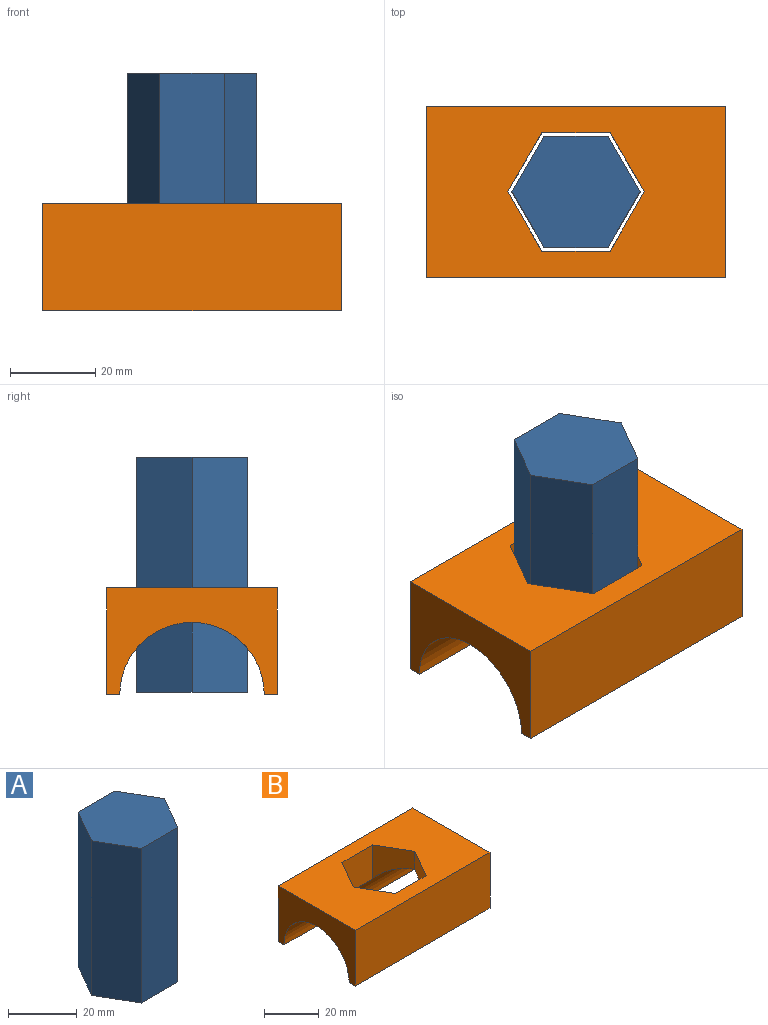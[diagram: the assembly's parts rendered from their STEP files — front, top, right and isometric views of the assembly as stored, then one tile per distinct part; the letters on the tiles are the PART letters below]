
ASSEMBLY  parts=2 mates=3
PART A: 8 faces, bbox 30x26x55 mm
  f0: plane 55x12.99mm, normal (0.87,-0.5,0), area 825mm2, adj f1,f5,f6,f7
  f1: plane 55x12.99mm, normal (0.87,0.5,0), area 825mm2, adj f0,f2,f6,f7
  f2: plane 55x15mm, normal (0,1,0), area 825mm2, adj f1,f3,f6,f7
  f3: plane 55x12.99mm, normal (-0.87,0.5,0), area 825mm2, adj f2,f4,f6,f7
  f4: plane 55x12.99mm, normal (-0.87,-0.5,0), area 825mm2, adj f3,f5,f6,f7
  f5: plane 55x15mm, normal (0,-1,0), area 825mm2, adj f0,f4,f6,f7
  f6: plane 30x25.98mm, normal (0,0,1), area 584.6mm2, adj f0,f1,f2,f3,f4,f5
  f7: plane 30x25.98mm, normal (0,0,-1), area 584.6mm2, adj f0,f1,f2,f3,f4,f5
PART B: 14 faces, bbox 70x40x25 mm
  f0: plane 70x3.08mm, normal (0,0,-1), area 215.4mm2, adj f6,f8,f9,f13
  f1: plane 15.28x13.86mm, normal (0.87,0.5,0), area 163.7mm2, adj f2,f10,f11,f13
  f2: plane 15.28x13.86mm, normal (0.87,-0.5,0), area 163.7mm2, adj f1,f3,f11,f13
  f3: plane 16x15.28mm, normal (0,-1,0), area 244.6mm2, adj f2,f4,f11,f13
  f4: plane 15.28x13.86mm, normal (-0.87,-0.5,0), area 163.7mm2, adj f3,f5,f11,f13
  f5: plane 15.28x13.86mm, normal (-0.87,0.5,0), area 163.7mm2, adj f4,f10,f11,f13
  f6: plane 40x25mm, normal (1,0,0), area 550.1mm2, adj f0,f7,f9,f11,f12,f13
  f7: plane 70x25mm, normal (0,1,0), area 1750mm2, adj f6,f8,f11,f12
  f8: plane 40x25mm, normal (-1,0,0), area 550.1mm2, adj f0,f7,f9,f11,f12,f13
  f9: plane 70x25mm, normal (0,-1,0), area 1750mm2, adj f0,f6,f8,f11
  f10: plane 16x15.28mm, normal (0,1,0), area 244.6mm2, adj f1,f5,f11,f13
  f11: plane 70x40mm, normal (0,0,1), area 2134.9mm2, adj f1,f2,f3,f4,f5,f6,f7,f8
  f12: plane 70x3.08mm, normal (0,0,-1), area 215.4mm2, adj f6,f7,f8,f13
  f13: cylinder r=16.92mm len=70mm, axis (1,0,0), area 2964.2mm2, adj f0,f1,f2,f3,f4,f5,f6,f8
PLACE A t=(0,0,0.56)mm
PLACE B at identity fixed
MATE parallel A.f0 <-> B.f5  axis (0.87,-0.5,0) through (15,0,0.56)mm
MATE slider A.f6 <-> B.f11  axis (0,0,1) through (0,0,55.56)mm
MATE parallel A.f5 <-> B.f10  axis (0,-1,0) through (0,-12.99,28.06)mm
